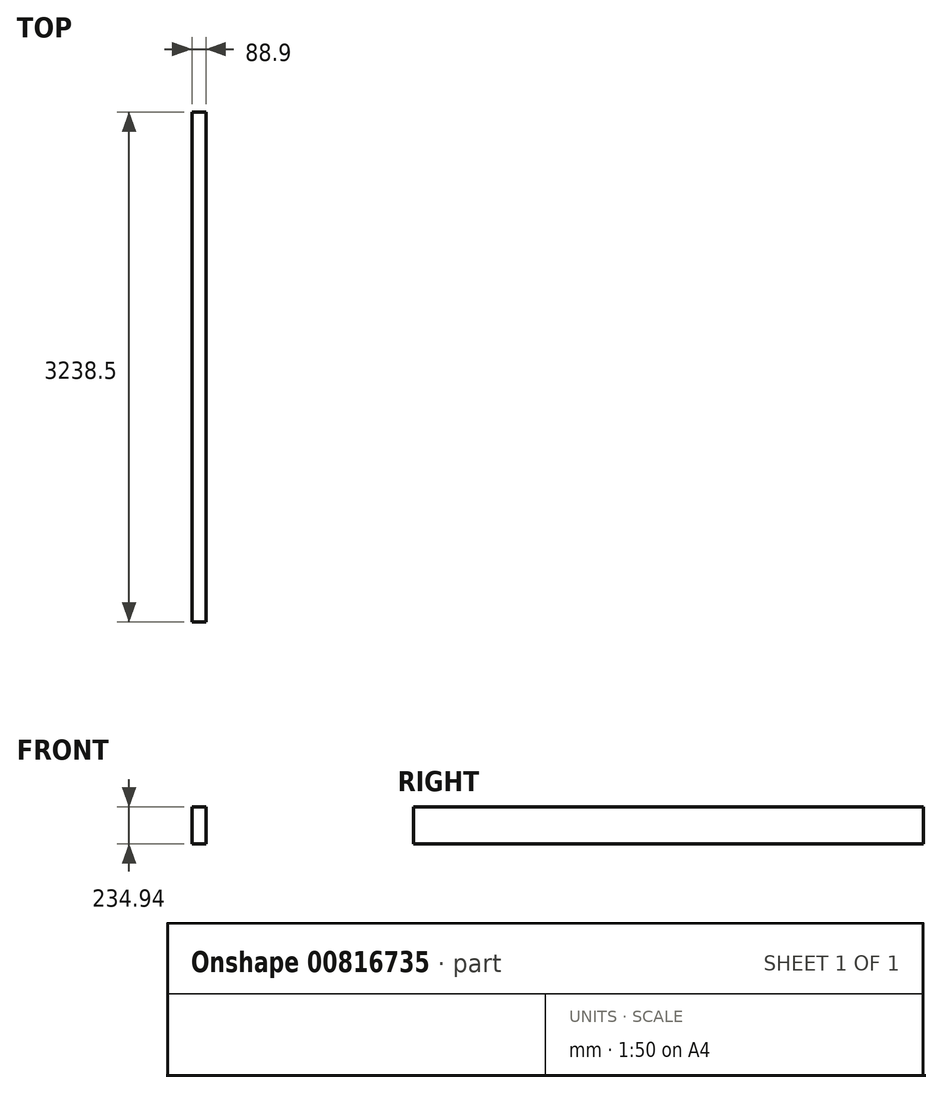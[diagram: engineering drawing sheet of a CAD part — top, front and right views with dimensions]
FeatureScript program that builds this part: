
annotation { "Feature Type Name" : "Feature", "Feature Type Description" : "" }
export const myFeature = defineFeature(function(context is Context, id is Id, definition is map)
    precondition{}
    {
        {
            var Q0;
            Q0=qCreatedBy(makeId("Front.planeOp"),FACE);
            var sketch = newSketch(context, id + "F0", { "sketchPlane" : qUnion([Q0])});
            skLineSegment(sketch, "E0.bottom", {"start": v(44.45, -117.48) * mm, "end": v(-44.45, -117.48) * mm});
            skLineSegment(sketch, "E0.top", {"start": v(44.45, 117.48) * mm, "end": v(-44.45, 117.48) * mm});
            skLineSegment(sketch, "E0.left", {"start": v(44.45, -117.48) * mm, "end": v(44.45, 117.47) * mm});
            skLineSegment(sketch, "E0.right", {"start": v(-44.45, -117.48) * mm, "end": v(-44.45, 117.48) * mm});
            skPoint(sketch, "E0.middle", {"position": v(0, 0) * mm});
            skSolve(sketch);
        }
        {
            var Q0;
            Q0 = qSketchRegion(id + "F0", true);
            extrude(context, id + "F1", {"entities" : qUnion([Q0]), "endBound" : BoundingType.SYMMETRIC, "depth" : 3238.5 * mm, "offsetDistance" : 25.4 * mm});
        }
    });
